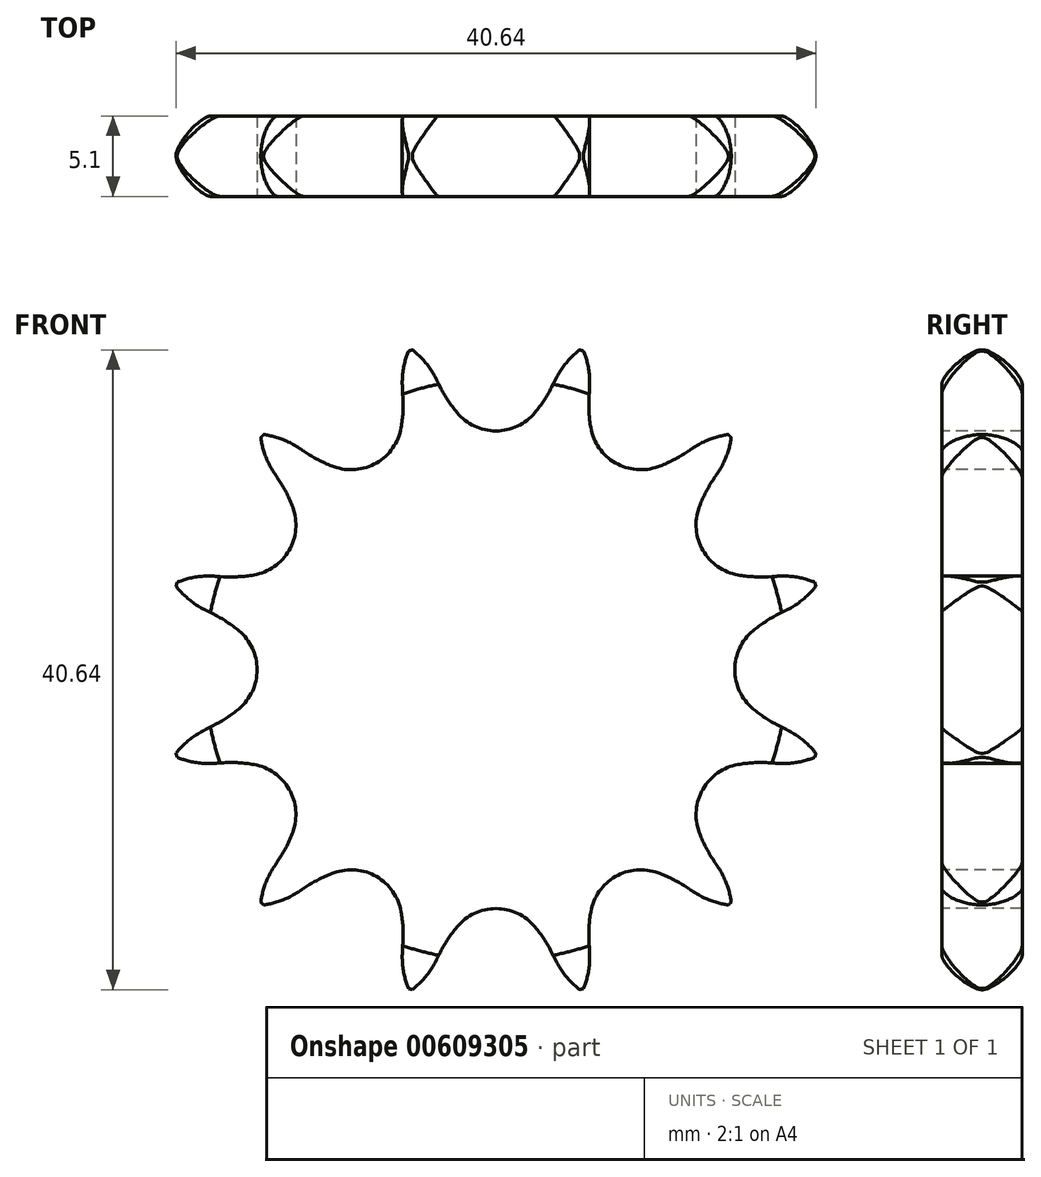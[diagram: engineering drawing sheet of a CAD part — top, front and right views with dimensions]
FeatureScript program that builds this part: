
annotation { "Feature Type Name" : "Feature", "Feature Type Description" : "" }
export const myFeature = defineFeature(function(context is Context, id is Id, definition is map)
    precondition{}
    {
        {
            var Q0;
            Q0=qCreatedBy(makeId("Right.planeOp"),FACE);
            var sketch = newSketch(context, id + "F0", { "sketchPlane" : qUnion([Q0])});
            skLineSegment(sketch, "E0", {"start": v(0, 0) * mm, "end": v(5.1, 0) * mm, "construction": true});
            skLineSegment(sketch, "E1", {"start": v(0, 21) * mm, "end": v(5.1, 21) * mm});
            skLineSegment(sketch, "E2", {"start": v(5.1, 21) * mm, "end": v(5.1, 15) * mm});
            skLineSegment(sketch, "E3", {"start": v(5.1, 15) * mm, "end": v(5.1, 15) * mm});
            skLineSegment(sketch, "E4", {"start": v(5.1, 15) * mm, "end": v(5.1, 0) * mm});
            skLineSegment(sketch, "E5", {"start": v(0, 0) * mm, "end": v(0, 21) * mm});
            skLineSegment(sketch, "E6.0.MirrorCS", {"start": v(0, -21) * mm, "end": v(5.1, -21) * mm});
            skLineSegment(sketch, "E6.1.MirrorCS", {"start": v(5.1, -21) * mm, "end": v(5.1, -15) * mm});
            skLineSegment(sketch, "E6.3.MirrorCS", {"start": v(5.1, -15) * mm, "end": v(5.1, 0) * mm});
            skLineSegment(sketch, "E6.4.MirrorCS", {"start": v(5.1, -15) * mm, "end": v(5.1, -15) * mm});
            skLineSegment(sketch, "E6.5.MirrorCS", {"start": v(0, 0) * mm, "end": v(0, -21) * mm});
            skLineSegment(sketch, "E7", {"start": v(0, 0) * mm, "end": v(5.1, 0) * mm});
            skSolve(sketch);
        }
        {
            var Q0;
            Q0=makeQuery(id+"F0.imprint","IMPRINT",FACE,{"disambiguationData":[TD([[makeQuery(id+"F0.imprint","IMPRINT",EDGE,{"derivedFrom":sQuery(id+"F0.wireOp",EDGE,"E1")}),-1.0]])]});
            var Q1;
            Q1=sQuery(id+"F0.wireOp",EDGE,"E0");
            revolve(context, id + "F1", {"entities" : qUnion([Q0]), "axis" : qUnion([Q1]), "revolveType" : RevolveType.FULL});
        }
        {
            var Q0;
            Q0=makeQuery(id+"F1.opRevolve","SWEPT_EDGE",EDGE,{"disambiguationData":[OSD([sQuery(id+"F0.wireOp",EDGE,"E1"),sQuery(id+"F0.wireOp",EDGE,"E5")])]});
            var Q1;
            Q1=makeQuery(id+"F1.opRevolve","SWEPT_EDGE",EDGE,{"disambiguationData":[OSD([sQuery(id+"F0.wireOp",EDGE,"E1"),sQuery(id+"F0.wireOp",EDGE,"E2")])]});
            fillet(context, id + "F2", {"entities" : qUnion([Q0, Q1]), "radius" : 2.5 * mm, "tangentPropagation" : true, "rho" : 0.2, "crossSection" : FilletCrossSection.CONIC, "allowEdgeOverflow" : false});
        }
        {
            var Q0;
            Q0=makeQuery(id+"F1.opRevolve","SWEPT_FACE",FACE,{"disambiguationData":[OSD([sQuery(id+"F0.wireOp",EDGE,"E5")])]});
            var sketch = newSketch(context, id + "F3", { "sketchPlane" : qUnion([Q0])});
            skArc(sketch, "E8", {"start": v(-5.48, 20.44) * mm, "mid": v(-12.65, 12.63) * mm, "end": v(-3.81, 18.5) * mm, "construction": true});
            skLineSegment(sketch, "E9", {"start": v(2.95, 5.03) * mm, "end": v(-3.81, 18.5) * mm, "construction": true});
            skArc(sketch, "E10", {"start": v(-2.47, 16.33) * mm, "mid": v(10.83, 26.23) * mm, "end": v(-3.53, 17.94) * mm, "construction": true});
            skArc(sketch, "E11", {"start": v(2.47, 16.33) * mm, "mid": v(0, 21.63) * mm, "end": v(-2.47, 16.33) * mm, "construction": true});
            skLineSegment(sketch, "E12", {"start": v(0, 0) * mm, "end": v(7.34, 0) * mm, "construction": true});
            skLineSegment(sketch, "E13", {"start": v(0, 18.4) * mm, "end": v(74.94, 18.4) * mm, "construction": true});
            skLineSegment(sketch, "E14", {"start": v(3.9, 21.67) * mm, "end": v(-3.53, 17.94) * mm, "construction": true});
            skLineSegment(sketch, "E15", {"start": v(0, 0) * mm, "end": v(-5.48, 20.44) * mm, "construction": true});
            skLineSegment(sketch, "E16", {"start": v(0, 0) * mm, "end": v(0, 18.4) * mm, "construction": true});
            skCircle(sketch, "E17", {"center": v(0, 0) * mm, "radius": 18.4 * mm, "construction": true});
            skLineSegment(sketch, "E18", {"start": v(0, 18.4) * mm, "end": v(3.9, 21.67) * mm, "construction": true});
            skArc(sketch, "E19", {"start": v(-2.47, 16.33) * mm, "mid": v(0, 15.17) * mm, "end": v(2.47, 16.33) * mm});
            skArc(sketch, "E20", {"start": v(-3.81, 18.5) * mm, "mid": v(-4.53, 19.57) * mm, "end": v(-5.48, 20.44) * mm});
            skArc(sketch, "E21.0.MirrorCS", {"start": v(3.53, 17.94) * mm, "mid": v(3.05, 17.1) * mm, "end": v(2.47, 16.33) * mm});
            skLineSegment(sketch, "E22.0.MirrorCS", {"start": v(3.53, 17.94) * mm, "end": v(3.81, 18.5) * mm});
            skArc(sketch, "E23.0.MirrorCS", {"start": v(3.81, 18.5) * mm, "mid": v(4.53, 19.57) * mm, "end": v(5.48, 20.44) * mm});
            skArc(sketch, "E24", {"start": v(-3.53, 17.94) * mm, "mid": v(-3.05, 17.1) * mm, "end": v(-2.47, 16.33) * mm});
            skLineSegment(sketch, "E25", {"start": v(-3.53, 17.94) * mm, "end": v(-3.81, 18.5) * mm});
            skArc(sketch, "E26.1.0", {"start": v(-12.55, 14.11) * mm, "mid": v(-13.7, 14.68) * mm, "end": v(-14.96, 14.96) * mm});
            skLineSegment(sketch, "E26.1.1", {"start": v(-12.03, 13.77) * mm, "end": v(-12.55, 14.11) * mm});
            skArc(sketch, "E26.1.2", {"start": v(-12.03, 13.77) * mm, "mid": v(-11.2, 13.28) * mm, "end": v(-10.3, 12.9) * mm});
            skArc(sketch, "E26.1.3", {"start": v(-10.3, 12.9) * mm, "mid": v(-7.59, 13.14) * mm, "end": v(-6.02, 15.37) * mm});
            skArc(sketch, "E26.1.4", {"start": v(-5.9, 17.3) * mm, "mid": v(-5.9, 16.33) * mm, "end": v(-6.02, 15.37) * mm});
            skLineSegment(sketch, "E26.1.5", {"start": v(-5.9, 17.3) * mm, "end": v(-5.95, 17.93) * mm});
            skArc(sketch, "E26.1.6", {"start": v(-5.95, 17.93) * mm, "mid": v(-5.86, 19.21) * mm, "end": v(-5.48, 20.44) * mm});
            skArc(sketch, "E26.2.0", {"start": v(-17.93, 5.95) * mm, "mid": v(-19.21, 5.86) * mm, "end": v(-20.44, 5.48) * mm});
            skLineSegment(sketch, "E26.2.1", {"start": v(-17.3, 5.9) * mm, "end": v(-17.93, 5.95) * mm});
            skArc(sketch, "E26.2.2", {"start": v(-17.3, 5.9) * mm, "mid": v(-16.33, 5.9) * mm, "end": v(-15.37, 6.02) * mm});
            skArc(sketch, "E26.2.3", {"start": v(-15.37, 6.02) * mm, "mid": v(-13.14, 7.59) * mm, "end": v(-12.9, 10.3) * mm});
            skArc(sketch, "E26.2.4", {"start": v(-13.77, 12.03) * mm, "mid": v(-13.28, 11.2) * mm, "end": v(-12.9, 10.3) * mm});
            skLineSegment(sketch, "E26.2.5", {"start": v(-13.77, 12.03) * mm, "end": v(-14.11, 12.55) * mm});
            skArc(sketch, "E26.2.6", {"start": v(-14.11, 12.55) * mm, "mid": v(-14.68, 13.7) * mm, "end": v(-14.96, 14.96) * mm});
            skArc(sketch, "E26.3.0", {"start": v(-18.5, -3.81) * mm, "mid": v(-19.57, -4.53) * mm, "end": v(-20.44, -5.48) * mm});
            skLineSegment(sketch, "E26.3.1", {"start": v(-17.94, -3.53) * mm, "end": v(-18.5, -3.81) * mm});
            skArc(sketch, "E26.3.2", {"start": v(-17.94, -3.53) * mm, "mid": v(-17.1, -3.05) * mm, "end": v(-16.33, -2.47) * mm});
            skArc(sketch, "E26.3.3", {"start": v(-16.33, -2.47) * mm, "mid": v(-15.17, 0) * mm, "end": v(-16.33, 2.47) * mm});
            skArc(sketch, "E26.3.4", {"start": v(-17.94, 3.53) * mm, "mid": v(-17.1, 3.05) * mm, "end": v(-16.33, 2.47) * mm});
            skLineSegment(sketch, "E26.3.5", {"start": v(-17.94, 3.53) * mm, "end": v(-18.5, 3.81) * mm});
            skArc(sketch, "E26.3.6", {"start": v(-18.5, 3.81) * mm, "mid": v(-19.57, 4.53) * mm, "end": v(-20.44, 5.48) * mm});
            skArc(sketch, "E26.4.0", {"start": v(-14.11, -12.55) * mm, "mid": v(-14.68, -13.7) * mm, "end": v(-14.96, -14.96) * mm});
            skLineSegment(sketch, "E26.4.1", {"start": v(-13.77, -12.03) * mm, "end": v(-14.11, -12.55) * mm});
            skArc(sketch, "E26.4.2", {"start": v(-13.77, -12.03) * mm, "mid": v(-13.28, -11.2) * mm, "end": v(-12.9, -10.3) * mm});
            skArc(sketch, "E26.4.3", {"start": v(-12.9, -10.3) * mm, "mid": v(-13.14, -7.59) * mm, "end": v(-15.37, -6.02) * mm});
            skArc(sketch, "E26.4.4", {"start": v(-17.3, -5.9) * mm, "mid": v(-16.33, -5.9) * mm, "end": v(-15.37, -6.02) * mm});
            skLineSegment(sketch, "E26.4.5", {"start": v(-17.3, -5.9) * mm, "end": v(-17.93, -5.95) * mm});
            skArc(sketch, "E26.4.6", {"start": v(-17.93, -5.95) * mm, "mid": v(-19.21, -5.86) * mm, "end": v(-20.44, -5.48) * mm});
            skArc(sketch, "E26.5.0", {"start": v(-5.95, -17.93) * mm, "mid": v(-5.86, -19.21) * mm, "end": v(-5.48, -20.44) * mm});
            skLineSegment(sketch, "E26.5.1", {"start": v(-5.9, -17.3) * mm, "end": v(-5.95, -17.93) * mm});
            skArc(sketch, "E26.5.2", {"start": v(-5.9, -17.3) * mm, "mid": v(-5.9, -16.33) * mm, "end": v(-6.02, -15.37) * mm});
            skArc(sketch, "E26.5.3", {"start": v(-6.02, -15.37) * mm, "mid": v(-7.59, -13.14) * mm, "end": v(-10.3, -12.9) * mm});
            skArc(sketch, "E26.5.4", {"start": v(-12.03, -13.77) * mm, "mid": v(-11.2, -13.28) * mm, "end": v(-10.3, -12.9) * mm});
            skLineSegment(sketch, "E26.5.5", {"start": v(-12.03, -13.77) * mm, "end": v(-12.55, -14.11) * mm});
            skArc(sketch, "E26.5.6", {"start": v(-12.55, -14.11) * mm, "mid": v(-13.7, -14.68) * mm, "end": v(-14.96, -14.96) * mm});
            skArc(sketch, "E26.6.0", {"start": v(3.81, -18.5) * mm, "mid": v(4.53, -19.57) * mm, "end": v(5.48, -20.44) * mm});
            skLineSegment(sketch, "E26.6.1", {"start": v(3.53, -17.94) * mm, "end": v(3.81, -18.5) * mm});
            skArc(sketch, "E26.6.2", {"start": v(3.53, -17.94) * mm, "mid": v(3.05, -17.1) * mm, "end": v(2.47, -16.33) * mm});
            skArc(sketch, "E26.6.3", {"start": v(2.47, -16.33) * mm, "mid": v(0, -15.17) * mm, "end": v(-2.47, -16.33) * mm});
            skArc(sketch, "E26.6.4", {"start": v(-3.53, -17.94) * mm, "mid": v(-3.05, -17.1) * mm, "end": v(-2.47, -16.33) * mm});
            skLineSegment(sketch, "E26.6.5", {"start": v(-3.53, -17.94) * mm, "end": v(-3.81, -18.5) * mm});
            skArc(sketch, "E26.6.6", {"start": v(-3.81, -18.5) * mm, "mid": v(-4.53, -19.57) * mm, "end": v(-5.48, -20.44) * mm});
            skArc(sketch, "E26.7.0", {"start": v(12.55, -14.11) * mm, "mid": v(13.7, -14.68) * mm, "end": v(14.96, -14.96) * mm});
            skLineSegment(sketch, "E26.7.1", {"start": v(12.03, -13.77) * mm, "end": v(12.55, -14.11) * mm});
            skArc(sketch, "E26.7.2", {"start": v(12.03, -13.77) * mm, "mid": v(11.2, -13.28) * mm, "end": v(10.3, -12.9) * mm});
            skArc(sketch, "E26.7.3", {"start": v(10.3, -12.9) * mm, "mid": v(7.59, -13.14) * mm, "end": v(6.02, -15.37) * mm});
            skArc(sketch, "E26.7.4", {"start": v(5.9, -17.3) * mm, "mid": v(5.9, -16.33) * mm, "end": v(6.02, -15.37) * mm});
            skLineSegment(sketch, "E26.7.5", {"start": v(5.9, -17.3) * mm, "end": v(5.95, -17.93) * mm});
            skArc(sketch, "E26.7.6", {"start": v(5.95, -17.93) * mm, "mid": v(5.86, -19.21) * mm, "end": v(5.48, -20.44) * mm});
            skArc(sketch, "E26.8.0", {"start": v(17.93, -5.95) * mm, "mid": v(19.21, -5.86) * mm, "end": v(20.44, -5.48) * mm});
            skLineSegment(sketch, "E26.8.1", {"start": v(17.3, -5.9) * mm, "end": v(17.93, -5.95) * mm});
            skArc(sketch, "E26.8.2", {"start": v(17.3, -5.9) * mm, "mid": v(16.33, -5.9) * mm, "end": v(15.37, -6.02) * mm});
            skArc(sketch, "E26.8.3", {"start": v(15.37, -6.02) * mm, "mid": v(13.14, -7.59) * mm, "end": v(12.9, -10.3) * mm});
            skArc(sketch, "E26.8.4", {"start": v(13.77, -12.03) * mm, "mid": v(13.28, -11.2) * mm, "end": v(12.9, -10.3) * mm});
            skLineSegment(sketch, "E26.8.5", {"start": v(13.77, -12.03) * mm, "end": v(14.11, -12.55) * mm});
            skArc(sketch, "E26.8.6", {"start": v(14.11, -12.55) * mm, "mid": v(14.68, -13.7) * mm, "end": v(14.96, -14.96) * mm});
            skArc(sketch, "E26.9.0", {"start": v(18.5, 3.81) * mm, "mid": v(19.57, 4.53) * mm, "end": v(20.44, 5.48) * mm});
            skLineSegment(sketch, "E26.9.1", {"start": v(17.94, 3.53) * mm, "end": v(18.5, 3.81) * mm});
            skArc(sketch, "E26.9.2", {"start": v(17.94, 3.53) * mm, "mid": v(17.1, 3.05) * mm, "end": v(16.33, 2.47) * mm});
            skArc(sketch, "E26.9.3", {"start": v(16.33, 2.47) * mm, "mid": v(15.17, 0) * mm, "end": v(16.33, -2.47) * mm});
            skArc(sketch, "E26.9.4", {"start": v(17.94, -3.53) * mm, "mid": v(17.1, -3.05) * mm, "end": v(16.33, -2.47) * mm});
            skLineSegment(sketch, "E26.9.5", {"start": v(17.94, -3.53) * mm, "end": v(18.5, -3.81) * mm});
            skArc(sketch, "E26.9.6", {"start": v(18.5, -3.81) * mm, "mid": v(19.57, -4.53) * mm, "end": v(20.44, -5.48) * mm});
            skArc(sketch, "E26.10.0", {"start": v(14.11, 12.55) * mm, "mid": v(14.68, 13.7) * mm, "end": v(14.96, 14.96) * mm});
            skLineSegment(sketch, "E26.10.1", {"start": v(13.77, 12.03) * mm, "end": v(14.11, 12.55) * mm});
            skArc(sketch, "E26.10.2", {"start": v(13.77, 12.03) * mm, "mid": v(13.28, 11.2) * mm, "end": v(12.9, 10.3) * mm});
            skArc(sketch, "E26.10.3", {"start": v(12.9, 10.3) * mm, "mid": v(13.14, 7.59) * mm, "end": v(15.37, 6.02) * mm});
            skArc(sketch, "E26.10.4", {"start": v(17.3, 5.9) * mm, "mid": v(16.33, 5.9) * mm, "end": v(15.37, 6.02) * mm});
            skLineSegment(sketch, "E26.10.5", {"start": v(17.3, 5.9) * mm, "end": v(17.93, 5.95) * mm});
            skArc(sketch, "E26.10.6", {"start": v(17.93, 5.95) * mm, "mid": v(19.21, 5.86) * mm, "end": v(20.44, 5.48) * mm});
            skArc(sketch, "E26.11.0", {"start": v(5.95, 17.93) * mm, "mid": v(5.86, 19.21) * mm, "end": v(5.48, 20.44) * mm});
            skLineSegment(sketch, "E26.11.1", {"start": v(5.9, 17.3) * mm, "end": v(5.95, 17.93) * mm});
            skArc(sketch, "E26.11.2", {"start": v(5.9, 17.3) * mm, "mid": v(5.9, 16.33) * mm, "end": v(6.02, 15.37) * mm});
            skArc(sketch, "E26.11.3", {"start": v(6.02, 15.37) * mm, "mid": v(7.59, 13.14) * mm, "end": v(10.3, 12.9) * mm});
            skArc(sketch, "E26.11.4", {"start": v(12.03, 13.77) * mm, "mid": v(11.2, 13.28) * mm, "end": v(10.3, 12.9) * mm});
            skLineSegment(sketch, "E26.11.5", {"start": v(12.03, 13.77) * mm, "end": v(12.55, 14.11) * mm});
            skArc(sketch, "E26.11.6", {"start": v(12.55, 14.11) * mm, "mid": v(13.7, 14.68) * mm, "end": v(14.96, 14.96) * mm});
            skSolve(sketch);
        }
        {
            var Q0;
            Q0=qSketchRegion(id+"F3",true);
            extrude(context, id + "F4", {"entities" : qUnion([Q0]), "operationType" : NewBodyOperationType.INTERSECT, "endBound" : BoundingType.THROUGH_ALL, "oppositeDirection" : true, "depth" : 25.4 * mm});
        }
    });
